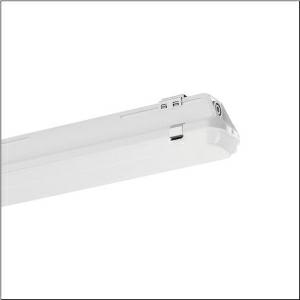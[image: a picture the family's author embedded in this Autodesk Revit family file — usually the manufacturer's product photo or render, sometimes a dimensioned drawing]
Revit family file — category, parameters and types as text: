
# Revit family: monsun_21_emergency_51fb20dl447k3h
name_source: partatom
category: Lighting Fixtures
units: mm (PartAtom-declared; Revit-internal decimal feet)

## family parameters
Cut with Voids When Loaded = No
Host = Face
Light Source = No
Part Type = Normal
Room Calculation Point = No
Round Connector Dimension = Use Diameter
Shared = No

## types (1)
- --- (1 x LED, 840 lm, 6.2 W, 4000K)
    Apparent Load = 6 VA
    CIE Flux Codes = 45 75 93 94 100
    Color Rendering = 80
    Color Temperature = 4000K
    Default Elevation = 1800 mm
    Description = Monsun 21 emergency, damp-proof luminaire, chain hanger, primary optical cover: enclosure, of PC, light emission: direct distribution, primary light characteristic: symmetric, installation type: vertical mounting, horizontal mounting, surface-mounted, suspended mounting, LED, rated luminous flux: 4.320lm, luminous efficacy: 162lm/W, light colour: 840, colour temperature: 4000K, control gear: DALI 2, with terminal, 5-pole, max. 2.5mm², mains connection: 220..240V, AC, 50/60Hz, rated input power: 30W, control gear: single battery element, battery: LiFePO4, 9Ah, housing, of glass-fibre reinforced plastic, uncoated, bright grey, incl. chain hanger, length: 1.299mm, width: 90mm, height: 88mm, clip for enclosure, of stainless steel (V2A), ceiling mounting element, of stainless steel (V2A), chain hanger, of stainless steel (V2A), protection rating (complete): IP66, insulation class (complete): insulation class I (protective earthing), certification: CE, UKCA, protection symbol: D, impact resistance: IK08, permissible operating ambient temperature: +5..+25°C, standard: EN 50419, EN 60598-2-1, corresponds to IFS (International Featured Standards) requirements for safety and quality in the food industry, for indoor or canopied outdoor use, no direct snow, no direct sun, no direct rain, LABS conformity tested according to VDMA 24364:2018-05, contact your sales advisor before using the luminaires in applications with unclear chemical exposure, large temperature fluctuations or condensation-forming humidity, packaging unit: 1 piece
    Height = 88 mm
    Lamp = 1 x LED
    Lamp Light Flux = 840 lm
    Lamp Power = 6.2 W
    Lamp count = 1
    Length = 1299 mm
    Luminous efficacy = 135 lm/W
    Manufacturer = Siteco
    ModVariant = No
    Model = 51FB20DL447K3H
    Mounting Place = Ceiling
    Mounting Type = Surface mounted
    Number of Poles = 1
    OnlyDefault = Yes
    Power Factor = 1
    Product Name = Monsun 21 emergency
    Product group = damp-proof luminaire
    ProductGroupID = 300
    Protection Class = Protection class I
    Protection Degree = IP 66
    RLX_Detail_Level = 1
    RLX_Emergency_Light_Flux = 0 lm
    RLX_Emergency_Type = 0
    RLX_Emergency_Type_DB = No
    RlxData = <blob elided: 93653 chars, md5=c1c2a271>
    Socket = socket
    Standby Power = 0 W
    System Light Flux = 840 lm
    System Power = 6 W
    Type Comments = : 3 h
    Type Image = l_1319656.jpg
    URL = http://relux.com
    VarID = @adj_037095
    Voltage = 0 V
    Weight = 0.00 kg
    Width = 90 mm

## geometry (parser evidence)
native form markers: Blend x4, Sweep x13
no freeform markers — native parametric forms only
